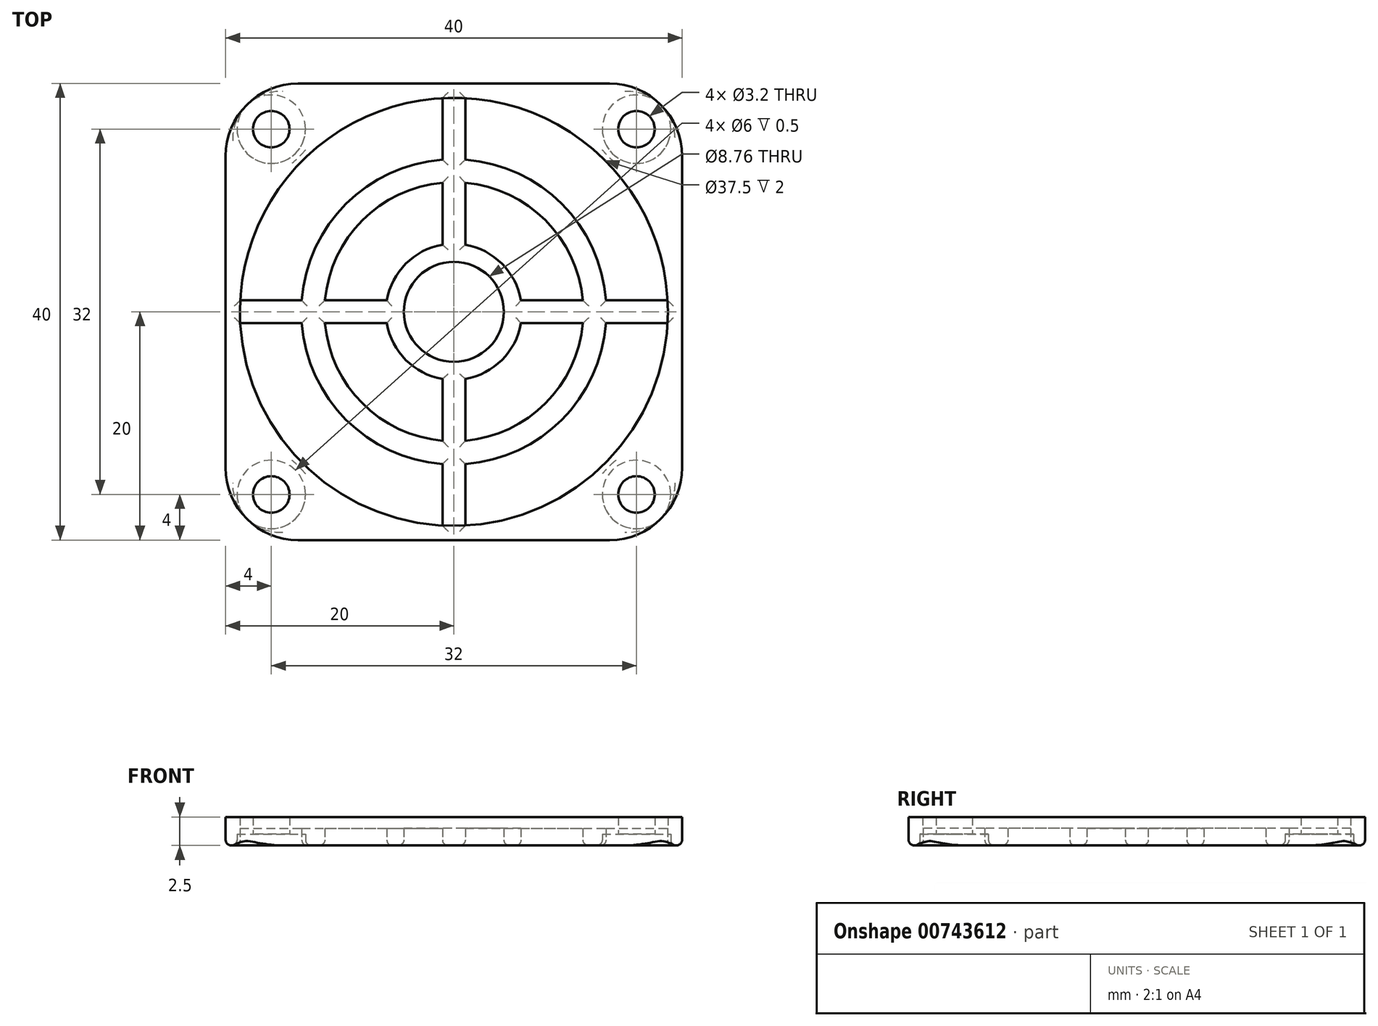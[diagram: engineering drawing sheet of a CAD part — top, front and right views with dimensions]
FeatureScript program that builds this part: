
annotation { "Feature Type Name" : "Feature", "Feature Type Description" : "" }
export const myFeature = defineFeature(function(context is Context, id is Id, definition is map)
    precondition{}
    {
        {
            var Q0;
            Q0=qCreatedBy(makeId("Top.planeOp"),FACE);
            var sketch = newSketch(context, id + "F0", { "sketchPlane" : qUnion([Q0])});
            skCircle(sketch, "E0", {"center": v(-16, 16) * mm, "radius": 1.6 * mm});
            skCircle(sketch, "E1", {"center": v(16, 16) * mm, "radius": 1.6 * mm});
            skCircle(sketch, "E2", {"center": v(16, -16) * mm, "radius": 1.6 * mm});
            skCircle(sketch, "E3", {"center": v(-16, -16) * mm, "radius": 1.6 * mm});
            skLineSegment(sketch, "E4.bottom", {"start": v(-13.65, 20) * mm, "end": v(13.65, 20) * mm});
            skLineSegment(sketch, "E4.top", {"start": v(-13.65, -20) * mm, "end": v(13.65, -20) * mm});
            skLineSegment(sketch, "E4.left", {"start": v(-20, 13.65) * mm, "end": v(-20, -13.65) * mm});
            skLineSegment(sketch, "E4.right", {"start": v(20, 13.65) * mm, "end": v(20, -13.65) * mm});
            skArc(sketch, "E5", {"start": v(-1, 18.72) * mm, "mid": v(-13.26, 13.26) * mm, "end": v(-18.72, 1) * mm});
            skLineSegment(sketch, "E6", {"start": v(-1, 18.72) * mm, "end": v(-1, 13.33) * mm});
            skLineSegment(sketch, "E7", {"start": v(1, 18.72) * mm, "end": v(1, 13.33) * mm});
            skLineSegment(sketch, "E8", {"start": v(-18.72, 1) * mm, "end": v(-13.33, 1) * mm});
            skLineSegment(sketch, "E9", {"start": v(-18.72, -1) * mm, "end": v(-13.33, -1) * mm});
            skArc(sketch, "E10.trimOffspring", {"start": v(18.72, 1) * mm, "mid": v(13.26, 13.26) * mm, "end": v(1, 18.72) * mm});
            skArc(sketch, "E11.trimOffspring", {"start": v(-18.72, -1) * mm, "mid": v(-13.26, -13.26) * mm, "end": v(-1, -18.72) * mm});
            skArc(sketch, "E12.trimOffspring", {"start": v(1, -18.72) * mm, "mid": v(13.26, -13.26) * mm, "end": v(18.72, -1) * mm});
            skArc(sketch, "E13", {"start": v(5.87, 1) * mm, "mid": v(4.21, 4.21) * mm, "end": v(1, 5.87) * mm});
            skArc(sketch, "E14", {"start": v(-1, 11.3) * mm, "mid": v(-8.02, 8.02) * mm, "end": v(-11.3, 1) * mm});
            skArc(sketch, "E15", {"start": v(-1, 13.33) * mm, "mid": v(-9.45, 9.45) * mm, "end": v(-13.33, 1) * mm});
            skLineSegment(sketch, "E16.trimOffspring", {"start": v(-1, 11.3) * mm, "end": v(-1, 5.87) * mm});
            skLineSegment(sketch, "E17.trimOffspring", {"start": v(1, 11.3) * mm, "end": v(1, 5.87) * mm});
            skLineSegment(sketch, "E18.trimOffspring", {"start": v(13.33, 1) * mm, "end": v(18.72, 1) * mm});
            skLineSegment(sketch, "E19.trimOffspring", {"start": v(13.33, -1) * mm, "end": v(18.72, -1) * mm});
            skArc(sketch, "E20.trimOffspring", {"start": v(11.3, 1) * mm, "mid": v(8.02, 8.02) * mm, "end": v(1, 11.3) * mm});
            skArc(sketch, "E21.trimOffspring", {"start": v(13.33, 1) * mm, "mid": v(9.45, 9.45) * mm, "end": v(1, 13.33) * mm});
            skLineSegment(sketch, "E22.trimOffspring", {"start": v(5.87, 1) * mm, "end": v(11.3, 1) * mm});
            skLineSegment(sketch, "E23.trimOffspring", {"start": v(5.87, -1) * mm, "end": v(11.3, -1) * mm});
            skArc(sketch, "E24.trimOffspring", {"start": v(1, -5.87) * mm, "mid": v(4.21, -4.21) * mm, "end": v(5.87, -1) * mm});
            skLineSegment(sketch, "E25.trimOffspring", {"start": v(1, -5.87) * mm, "end": v(1, -11.3) * mm});
            skLineSegment(sketch, "E26.trimOffspring", {"start": v(-1, -5.87) * mm, "end": v(-1, -11.3) * mm});
            skArc(sketch, "E27.trimOffspring", {"start": v(-5.87, -1) * mm, "mid": v(-4.21, -4.21) * mm, "end": v(-1, -5.87) * mm});
            skLineSegment(sketch, "E28.trimOffspring", {"start": v(-11.3, 1) * mm, "end": v(-5.87, 1) * mm});
            skArc(sketch, "E29.trimOffspring", {"start": v(-11.3, -1) * mm, "mid": v(-8.02, -8.02) * mm, "end": v(-1, -11.3) * mm});
            skArc(sketch, "E30.trimOffspring", {"start": v(-13.33, -1) * mm, "mid": v(-9.45, -9.45) * mm, "end": v(-1, -13.33) * mm});
            skLineSegment(sketch, "E31.trimOffspring", {"start": v(-11.3, -1) * mm, "end": v(-5.87, -1) * mm});
            skArc(sketch, "E32.trimOffspring", {"start": v(1, -11.3) * mm, "mid": v(8.02, -8.02) * mm, "end": v(11.3, -1) * mm});
            skArc(sketch, "E33.trimOffspring", {"start": v(1, -13.33) * mm, "mid": v(9.45, -9.45) * mm, "end": v(13.33, -1) * mm});
            skLineSegment(sketch, "E34.trimOffspring", {"start": v(1, -13.33) * mm, "end": v(1, -18.72) * mm});
            skLineSegment(sketch, "E35.trimOffspring", {"start": v(-1, -13.33) * mm, "end": v(-1, -18.72) * mm});
            skArc(sketch, "E36.trimOffspring", {"start": v(-1, 5.87) * mm, "mid": v(-4.21, 4.21) * mm, "end": v(-5.87, 1) * mm});
            skCircle(sketch, "E37", {"center": v(0, 0) * mm, "radius": 4.38 * mm});
            skPoint(sketch, "E38.visualSharp", {"position": v(-20, 20) * mm});
            skArc(sketch, "E38.filletArc", {"start": v(-13.65, 20) * mm, "mid": v(-18.14, 18.14) * mm, "end": v(-20, 13.65) * mm});
            skPoint(sketch, "E39.visualSharp", {"position": v(-20, -20) * mm});
            skArc(sketch, "E39.filletArc", {"start": v(-20, -13.65) * mm, "mid": v(-18.14, -18.14) * mm, "end": v(-13.65, -20) * mm});
            skPoint(sketch, "E40.visualSharp", {"position": v(20, -20) * mm});
            skArc(sketch, "E40.filletArc", {"start": v(13.65, -20) * mm, "mid": v(18.14, -18.14) * mm, "end": v(20, -13.65) * mm});
            skPoint(sketch, "E41.visualSharp", {"position": v(20, 20) * mm});
            skArc(sketch, "E41.filletArc", {"start": v(20, 13.65) * mm, "mid": v(18.14, 18.14) * mm, "end": v(13.65, 20) * mm});
            skSolve(sketch);
        }
        {
            var Q0;
            Q0 = qSketchRegion(id + "F0", true);
            extrude(context, id + "F1", {"entities" : qUnion([Q0]), "depth" : 2.5 * mm, "offsetDistance" : 25.4 * mm});
        }
        {
            var Q0;
            Q0=makeQuery(id+"F1.opExtrude","CAP_FACE",FACE,{"disambiguationData":[OSD([sQuery(id+"F0.wireOp",EDGE,"E0"),sQuery(id+"F0.wireOp",EDGE,"E1"),sQuery(id+"F0.wireOp",EDGE,"E2"),sQuery(id+"F0.wireOp",EDGE,"E3"),sQuery(id+"F0.wireOp",EDGE,"E4.bottom"),sQuery(id+"F0.wireOp",EDGE,"E4.top"),sQuery(id+"F0.wireOp",EDGE,"E4.left"),sQuery(id+"F0.wireOp",EDGE,"E4.right"),sQuery(id+"F0.wireOp",EDGE,"E5"),sQuery(id+"F0.wireOp",EDGE,"E6"),sQuery(id+"F0.wireOp",EDGE,"E7"),sQuery(id+"F0.wireOp",EDGE,"E8"),sQuery(id+"F0.wireOp",EDGE,"E9"),sQuery(id+"F0.wireOp",EDGE,"3f5c4570-0d0e-4342-8f31-e9b691c76b48.trimOffspring"),sQuery(id+"F0.wireOp",EDGE,"b0981ca9-4a93-40c7-8ede-b21ccdf9ea9c.trimOffspring"),sQuery(id+"F0.wireOp",EDGE,"156f85e7-4a59-4eaa-8c94-7897f76e2177.trimOffspring"),sQuery(id+"F0.wireOp",EDGE,"7a4ee4ac-a209-40c9-a21d-254fe2efd8aa.trimOffspring"),sQuery(id+"F0.wireOp",EDGE,"E10.trimOffspring"),sQuery(id+"F0.wireOp",EDGE,"E11.trimOffspring"),sQuery(id+"F0.wireOp",EDGE,"E12.trimOffspring"),sQuery(id+"F0.wireOp",EDGE,"hUL42VZN-iO2z-RDmx-ddcc-wAsxaYuwDb2i"),sQuery(id+"F0.wireOp",EDGE,"E13"),sQuery(id+"F0.wireOp",EDGE,"E14"),sQuery(id+"F0.wireOp",EDGE,"E15"),sQuery(id+"F0.wireOp",EDGE,"E16.trimOffspring"),sQuery(id+"F0.wireOp",EDGE,"E17.trimOffspring"),sQuery(id+"F0.wireOp",EDGE,"E18.trimOffspring"),sQuery(id+"F0.wireOp",EDGE,"E19.trimOffspring"),sQuery(id+"F0.wireOp",EDGE,"E20.trimOffspring"),sQuery(id+"F0.wireOp",EDGE,"E21.trimOffspring"),sQuery(id+"F0.wireOp",EDGE,"E22.trimOffspring"),sQuery(id+"F0.wireOp",EDGE,"E23.trimOffspring"),sQuery(id+"F0.wireOp",EDGE,"E24.trimOffspring"),sQuery(id+"F0.wireOp",EDGE,"5baa72d9-31dc-45eb-b5c1-436ed97127be.trimOffspring"),sQuery(id+"F0.wireOp",EDGE,"E25.trimOffspring"),sQuery(id+"F0.wireOp",EDGE,"E26.trimOffspring"),sQuery(id+"F0.wireOp",EDGE,"923efe1c-8501-4d4e-8851-86086e94e9f1.trimOffspring"),sQuery(id+"F0.wireOp",EDGE,"3f79d5fb-0a8b-4b1f-bc07-6d58af1cd0cc.trimOffspring"),sQuery(id+"F0.wireOp",EDGE,"E27.trimOffspring"),sQuery(id+"F0.wireOp",EDGE,"26bf0d5e-ea2e-47a8-97aa-4e4c95460ec9.trimOffspring"),sQuery(id+"F0.wireOp",EDGE,"E28.trimOffspring"),sQuery(id+"F0.wireOp",EDGE,"E29.trimOffspring"),sQuery(id+"F0.wireOp",EDGE,"E30.trimOffspring"),sQuery(id+"F0.wireOp",EDGE,"E31.trimOffspring"),sQuery(id+"F0.wireOp",EDGE,"E32.trimOffspring"),sQuery(id+"F0.wireOp",EDGE,"E33.trimOffspring"),sQuery(id+"F0.wireOp",EDGE,"E34.trimOffspring"),sQuery(id+"F0.wireOp",EDGE,"E35.trimOffspring"),sQuery(id+"F0.wireOp",EDGE,"E36.trimOffspring"),sQuery(id+"F0.wireOp",EDGE,"6d97bbf4-c9fc-463e-bf00-e0ef0d70c1c3.trimOffspring"),sQuery(id+"F0.wireOp",EDGE,"3c499df6-884c-4b4b-8284-fedb37a8e2a6.trimOffspring"),sQuery(id+"F0.wireOp",EDGE,"9bf78612-3a2b-4ab4-ae83-326c1b6aaf60.trimOffspring")])],"isStart":false});
            var sketch = newSketch(context, id + "F2", { "sketchPlane" : qUnion([Q0])});
            skArc(sketch, "E42.0", {"start": v(-1, 18.72) * mm, "mid": v(-13.26, 13.26) * mm, "end": v(-18.72, 1) * mm});
            skArc(sketch, "E43.0", {"start": v(-18.72, -1) * mm, "mid": v(-13.26, -13.26) * mm, "end": v(-1, -18.72) * mm});
            skCircle(sketch, "E44", {"center": v(0, 0) * mm, "radius": 18.75 * mm});
            skSolve(sketch);
        }
        {
            var Q0;
            Q0 = qSketchRegion(id + "F2", true);
            extrude(context, id + "F3", {"entities" : qUnion([Q0]), "operationType" : NewBodyOperationType.REMOVE, "oppositeDirection" : true, "depth" : 1 * mm, "offsetDistance" : 25.4 * mm});
        }
        {
            var Q0;
            Q0=makeQuery(id+"F1.opExtrude","CAP_FACE",FACE,{"disambiguationData":[OSD([sQuery(id+"F0.wireOp",EDGE,"E0"),sQuery(id+"F0.wireOp",EDGE,"E1"),sQuery(id+"F0.wireOp",EDGE,"E2"),sQuery(id+"F0.wireOp",EDGE,"E3"),sQuery(id+"F0.wireOp",EDGE,"E4.bottom"),sQuery(id+"F0.wireOp",EDGE,"E4.top"),sQuery(id+"F0.wireOp",EDGE,"E4.left"),sQuery(id+"F0.wireOp",EDGE,"E4.right"),sQuery(id+"F0.wireOp",EDGE,"E5"),sQuery(id+"F0.wireOp",EDGE,"E6"),sQuery(id+"F0.wireOp",EDGE,"E7"),sQuery(id+"F0.wireOp",EDGE,"E8"),sQuery(id+"F0.wireOp",EDGE,"E9"),sQuery(id+"F0.wireOp",EDGE,"3f5c4570-0d0e-4342-8f31-e9b691c76b48.trimOffspring"),sQuery(id+"F0.wireOp",EDGE,"b0981ca9-4a93-40c7-8ede-b21ccdf9ea9c.trimOffspring"),sQuery(id+"F0.wireOp",EDGE,"156f85e7-4a59-4eaa-8c94-7897f76e2177.trimOffspring"),sQuery(id+"F0.wireOp",EDGE,"7a4ee4ac-a209-40c9-a21d-254fe2efd8aa.trimOffspring"),sQuery(id+"F0.wireOp",EDGE,"E10.trimOffspring"),sQuery(id+"F0.wireOp",EDGE,"E11.trimOffspring"),sQuery(id+"F0.wireOp",EDGE,"E12.trimOffspring"),sQuery(id+"F0.wireOp",EDGE,"hUL42VZN-iO2z-RDmx-ddcc-wAsxaYuwDb2i"),sQuery(id+"F0.wireOp",EDGE,"E13"),sQuery(id+"F0.wireOp",EDGE,"E14"),sQuery(id+"F0.wireOp",EDGE,"E15"),sQuery(id+"F0.wireOp",EDGE,"E16.trimOffspring"),sQuery(id+"F0.wireOp",EDGE,"E17.trimOffspring"),sQuery(id+"F0.wireOp",EDGE,"E18.trimOffspring"),sQuery(id+"F0.wireOp",EDGE,"E19.trimOffspring"),sQuery(id+"F0.wireOp",EDGE,"E20.trimOffspring"),sQuery(id+"F0.wireOp",EDGE,"E21.trimOffspring"),sQuery(id+"F0.wireOp",EDGE,"E22.trimOffspring"),sQuery(id+"F0.wireOp",EDGE,"E23.trimOffspring"),sQuery(id+"F0.wireOp",EDGE,"E24.trimOffspring"),sQuery(id+"F0.wireOp",EDGE,"5baa72d9-31dc-45eb-b5c1-436ed97127be.trimOffspring"),sQuery(id+"F0.wireOp",EDGE,"E25.trimOffspring"),sQuery(id+"F0.wireOp",EDGE,"E26.trimOffspring"),sQuery(id+"F0.wireOp",EDGE,"923efe1c-8501-4d4e-8851-86086e94e9f1.trimOffspring"),sQuery(id+"F0.wireOp",EDGE,"3f79d5fb-0a8b-4b1f-bc07-6d58af1cd0cc.trimOffspring"),sQuery(id+"F0.wireOp",EDGE,"E27.trimOffspring"),sQuery(id+"F0.wireOp",EDGE,"26bf0d5e-ea2e-47a8-97aa-4e4c95460ec9.trimOffspring"),sQuery(id+"F0.wireOp",EDGE,"E28.trimOffspring"),sQuery(id+"F0.wireOp",EDGE,"E29.trimOffspring"),sQuery(id+"F0.wireOp",EDGE,"E30.trimOffspring"),sQuery(id+"F0.wireOp",EDGE,"E31.trimOffspring"),sQuery(id+"F0.wireOp",EDGE,"E32.trimOffspring"),sQuery(id+"F0.wireOp",EDGE,"E33.trimOffspring"),sQuery(id+"F0.wireOp",EDGE,"E34.trimOffspring"),sQuery(id+"F0.wireOp",EDGE,"E35.trimOffspring"),sQuery(id+"F0.wireOp",EDGE,"E36.trimOffspring"),sQuery(id+"F0.wireOp",EDGE,"6d97bbf4-c9fc-463e-bf00-e0ef0d70c1c3.trimOffspring"),sQuery(id+"F0.wireOp",EDGE,"3c499df6-884c-4b4b-8284-fedb37a8e2a6.trimOffspring"),sQuery(id+"F0.wireOp",EDGE,"9bf78612-3a2b-4ab4-ae83-326c1b6aaf60.trimOffspring")])],"isStart":true});
            var sketch = newSketch(context, id + "F4", { "sketchPlane" : qUnion([Q0])});
            skCircle(sketch, "E45.0", {"center": v(-16, -16) * mm, "radius": 1.6 * mm});
            skCircle(sketch, "E46.0", {"center": v(16, -16) * mm, "radius": 1.6 * mm});
            skCircle(sketch, "E47.0", {"center": v(16, 16) * mm, "radius": 1.6 * mm});
            skCircle(sketch, "E48.0", {"center": v(-16, 16) * mm, "radius": 1.6 * mm});
            skCircle(sketch, "E49", {"center": v(-16, 16) * mm, "radius": 3 * mm});
            skCircle(sketch, "E50", {"center": v(16, 16) * mm, "radius": 3 * mm});
            skCircle(sketch, "E51", {"center": v(16, -16) * mm, "radius": 3 * mm});
            skCircle(sketch, "E52", {"center": v(-16, -16) * mm, "radius": 3 * mm});
            skSolve(sketch);
        }
        {
            var Q0;
            Q0 = qSketchRegion(id + "F4", true);
            extrude(context, id + "F5", {"entities" : qUnion([Q0]), "operationType" : NewBodyOperationType.REMOVE, "oppositeDirection" : true, "depth" : 1 * mm, "offsetDistance" : 25.4 * mm});
        }
        {
            var Q0;
            Q0=makeQuery(id+"F1.opExtrude","CAP_FACE",FACE,{"disambiguationData":[OSD([sQuery(id+"F0.wireOp",EDGE,"E0"),sQuery(id+"F0.wireOp",EDGE,"E1"),sQuery(id+"F0.wireOp",EDGE,"E2"),sQuery(id+"F0.wireOp",EDGE,"E3"),sQuery(id+"F0.wireOp",EDGE,"E4.bottom"),sQuery(id+"F0.wireOp",EDGE,"E4.top"),sQuery(id+"F0.wireOp",EDGE,"E4.left"),sQuery(id+"F0.wireOp",EDGE,"E4.right"),sQuery(id+"F0.wireOp",EDGE,"E5"),sQuery(id+"F0.wireOp",EDGE,"E6"),sQuery(id+"F0.wireOp",EDGE,"E7"),sQuery(id+"F0.wireOp",EDGE,"E8"),sQuery(id+"F0.wireOp",EDGE,"E9"),sQuery(id+"F0.wireOp",EDGE,"E10.trimOffspring"),sQuery(id+"F0.wireOp",EDGE,"E11.trimOffspring"),sQuery(id+"F0.wireOp",EDGE,"E12.trimOffspring"),sQuery(id+"F0.wireOp",EDGE,"E13"),sQuery(id+"F0.wireOp",EDGE,"E14"),sQuery(id+"F0.wireOp",EDGE,"E15"),sQuery(id+"F0.wireOp",EDGE,"E16.trimOffspring"),sQuery(id+"F0.wireOp",EDGE,"E17.trimOffspring"),sQuery(id+"F0.wireOp",EDGE,"E18.trimOffspring"),sQuery(id+"F0.wireOp",EDGE,"E19.trimOffspring"),sQuery(id+"F0.wireOp",EDGE,"E20.trimOffspring"),sQuery(id+"F0.wireOp",EDGE,"E21.trimOffspring"),sQuery(id+"F0.wireOp",EDGE,"E22.trimOffspring"),sQuery(id+"F0.wireOp",EDGE,"E23.trimOffspring"),sQuery(id+"F0.wireOp",EDGE,"E24.trimOffspring"),sQuery(id+"F0.wireOp",EDGE,"E25.trimOffspring"),sQuery(id+"F0.wireOp",EDGE,"E26.trimOffspring"),sQuery(id+"F0.wireOp",EDGE,"E27.trimOffspring"),sQuery(id+"F0.wireOp",EDGE,"E28.trimOffspring"),sQuery(id+"F0.wireOp",EDGE,"E29.trimOffspring"),sQuery(id+"F0.wireOp",EDGE,"E30.trimOffspring"),sQuery(id+"F0.wireOp",EDGE,"E31.trimOffspring"),sQuery(id+"F0.wireOp",EDGE,"E32.trimOffspring"),sQuery(id+"F0.wireOp",EDGE,"E33.trimOffspring"),sQuery(id+"F0.wireOp",EDGE,"E34.trimOffspring"),sQuery(id+"F0.wireOp",EDGE,"E35.trimOffspring"),sQuery(id+"F0.wireOp",EDGE,"E36.trimOffspring"),sQuery(id+"F0.wireOp",EDGE,"E37"),sQuery(id+"F0.wireOp",EDGE,"E38.filletArc"),sQuery(id+"F0.wireOp",EDGE,"E39.filletArc"),sQuery(id+"F0.wireOp",EDGE,"E40.filletArc"),sQuery(id+"F0.wireOp",EDGE,"E41.filletArc")])],"isStart":true});
            fillet(context, id + "F6", {"entities" : qUnion([Q0]), "tangentPropagation" : true, "radius" : .5 * mm, "defaultsChanged" : true, "vertexSettings" : [], "allowEdgeOverflow" : false});
        }
    });
